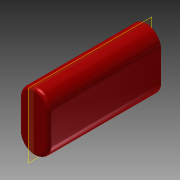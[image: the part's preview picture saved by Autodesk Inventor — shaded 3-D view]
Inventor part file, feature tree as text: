
AUTODESK INVENTOR PART (.ipt)
format: ipt  version: 2014 SP1 (Build 180222100, 222)  size: 93,696 bytes
history: native  units: mm (DEFAULTED — no unit token found)
features: plane x2, extrude x1, fillet x1, sketch x1, reference x1
ambient origin geometry x8: Origin, YZ Plane, XZ Plane, XY Plane, X Axis, Y Axis, Z Axis, Center Point
bodies: Solid1 (feature_tree)
feature tree (6):
  extrude  "Extrusion1"  Depth=0.381mm
  fillet  "Fillet1"  [1 undecoded]
  plane  "Work Plane1"
  plane  "Work Plane2"
  sketch  "Sketch1"  dims[d0=12.7mm d1=0.0mm d2=0.381mm]
  reference  "Reference1"
note: 1 required parameter value undecoded (feature->parameter linkage not recoverable at this tier; creation-order binding heuristic only, values carry confidence <= 0.55)
